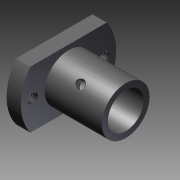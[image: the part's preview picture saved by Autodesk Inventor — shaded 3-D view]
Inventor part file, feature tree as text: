
AUTODESK INVENTOR PART (.ipt)
format: ipt  version: 2011 SP1 (Build 150282100, 282)  size: 157,696 bytes
history: native  units: mm
features: other x14, sketch x6, revolve x5, thread x4, extrude x1
ambient origin geometry x8: Origin, YZ Plane, XZ Plane, XY Plane, X Axis, Y Axis, Z Axis, Center Point
bodies: Solid1 (feature_tree)
feature tree (30):
  revolve  "Revolution1"  Angle=360.0deg
  revolve  "Revolution2"  Angle=360.0deg
  thread  "Thread1"  [1 undecoded]
  revolve  "Revolution3"  Angle=360.0deg
  thread  "Thread2"  [1 undecoded]
  extrude  "Extrusion1"  Depth=5.242mm TaperAngle=0.0deg
  revolve  "Revolution4"  [1 undecoded]
  thread  "Thread3"  [1 undecoded]
  revolve  "Revolution5"  [1 undecoded]
  thread  "Thread4"  [1 undecoded]
  other  "to_screw1_XY"
  other  "to_screw1_YZ"
  other  "to_screw1_ZX"
  other  "to_screw1_X"
  other  "to_screw1_Y"
  other  "to_screw1_Z"
  other  "to_screw1_Center"
  other  "to_screw2_XY"
  other  "to_screw2_YZ"
  other  "to_screw2_ZX"
  other  "to_screw2_X"
  other  "to_screw2_Y"
  other  "to_screw2_Z"
  other  "to_screw2_Center"
  sketch  "Sketch_1"  dims[d0=360.0deg d1=360.0deg]
  sketch  "Sketch_3"  dims[d7=30.0mm d8=0.0mm d9=360.0deg d10=5.242mm d11=0.0mm]
  sketch  "Sketch_2"  dims[d2=2.39258mm d3=0.0mm d4=360.0deg d5=2.39258mm d6=0.0mm]
  sketch  "Sketch_4"  dims[d12=360.0deg d13=5.242mm d14=0.0mm]
  sketch  "Sketch_12"
  sketch  "Sketch_14"
note: 6 required parameter values undecoded (feature->parameter linkage not recoverable at this tier; creation-order binding heuristic only, values carry confidence <= 0.55)
